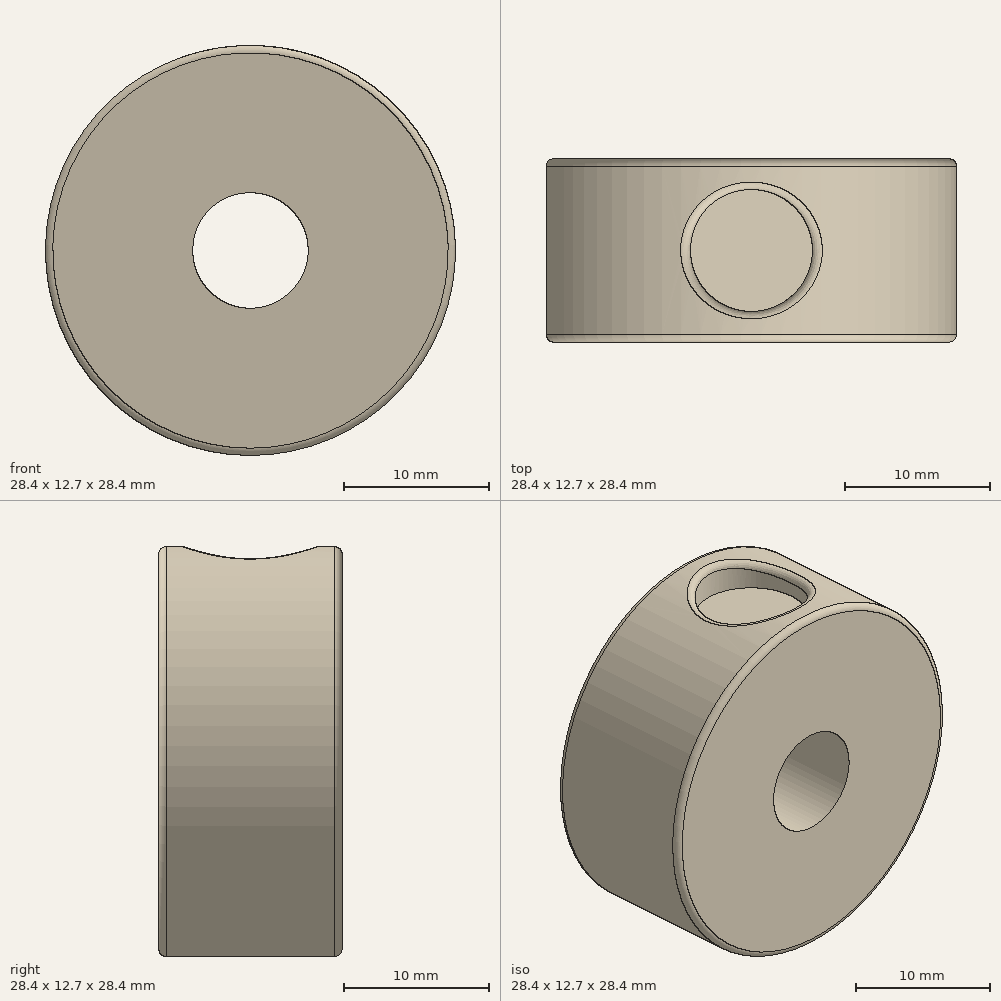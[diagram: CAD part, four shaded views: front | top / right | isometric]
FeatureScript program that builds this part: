
annotation { "Feature Type Name" : "Feature", "Feature Type Description" : "" }
export const myFeature = defineFeature(function(context is Context, id is Id, definition is map)
    precondition{}
    {
        {
            var Q0;
            Q0=qCreatedBy(makeId("Front.planeOp"),FACE);
            var sketch = newSketch(context, id + "F0", { "sketchPlane" : qUnion([Q0])});
            skCircle(sketch, "E0.cCircle", {"center": v(0, 0) * mm, "radius": 12.21 * mm, "construction": true});
            skLineSegment(sketch, "E0.0", {"start": v(-3.97, 12.21) * mm, "end": v(3.97, 12.21) * mm, "construction": true});
            skLineSegment(sketch, "E0.1", {"start": v(3.97, 12.21) * mm, "end": v(10.4, 7.55) * mm, "construction": true});
            skLineSegment(sketch, "E0.2", {"start": v(10.4, 7.55) * mm, "end": v(12.84, 0) * mm, "construction": true});
            skLineSegment(sketch, "E0.3", {"start": v(12.84, 0) * mm, "end": v(10.4, -7.55) * mm, "construction": true});
            skLineSegment(sketch, "E0.4", {"start": v(10.4, -7.55) * mm, "end": v(3.97, -12.21) * mm, "construction": true});
            skLineSegment(sketch, "E0.5", {"start": v(3.97, -12.21) * mm, "end": v(-3.97, -12.21) * mm, "construction": true});
            skLineSegment(sketch, "E0.6", {"start": v(-3.97, -12.21) * mm, "end": v(-10.4, -7.55) * mm, "construction": true});
            skLineSegment(sketch, "E0.7", {"start": v(-10.4, -7.55) * mm, "end": v(-12.84, 0) * mm, "construction": true});
            skLineSegment(sketch, "E0.8", {"start": v(-12.84, 0) * mm, "end": v(-10.4, 7.55) * mm, "construction": true});
            skLineSegment(sketch, "E0.9", {"start": v(-10.4, 7.55) * mm, "end": v(-3.97, 12.21) * mm, "construction": true});
            skPoint(sketch, "E0.0.midPoint", {"position": v(0, 12.21) * mm});
            skCircle(sketch, "E1.cCircle", {"center": v(0, 0) * mm, "radius": 14.2 * mm});
            skLineSegment(sketch, "E1.0", {"start": v(-4.61, 14.2) * mm, "end": v(4.61, 14.2) * mm, "construction": true});
            skLineSegment(sketch, "E1.1", {"start": v(4.61, 14.2) * mm, "end": v(12.08, 8.78) * mm, "construction": true});
            skLineSegment(sketch, "E1.2", {"start": v(12.08, 8.78) * mm, "end": v(14.93, 0) * mm, "construction": true});
            skLineSegment(sketch, "E1.3", {"start": v(14.93, 0) * mm, "end": v(12.08, -8.78) * mm, "construction": true});
            skLineSegment(sketch, "E1.4", {"start": v(12.08, -8.78) * mm, "end": v(4.61, -14.2) * mm, "construction": true});
            skLineSegment(sketch, "E1.5", {"start": v(4.61, -14.2) * mm, "end": v(-4.61, -14.2) * mm, "construction": true});
            skLineSegment(sketch, "E1.6", {"start": v(-4.61, -14.2) * mm, "end": v(-12.08, -8.78) * mm, "construction": true});
            skLineSegment(sketch, "E1.7", {"start": v(-12.08, -8.78) * mm, "end": v(-14.93, 0) * mm, "construction": true});
            skLineSegment(sketch, "E1.8", {"start": v(-14.93, 0) * mm, "end": v(-12.08, 8.78) * mm, "construction": true});
            skLineSegment(sketch, "E1.9", {"start": v(-12.08, 8.78) * mm, "end": v(-4.61, 14.2) * mm, "construction": true});
            skPoint(sketch, "E1.0.midPoint", {"position": v(0, 14.2) * mm});
            skCircle(sketch, "E2", {"center": v(0, 0) * mm, "radius": 4 * mm});
            skSolve(sketch);
        }
        {
            var Q0;
            Q0=qSketchRegion(id+"F0",true);
            extrude(context, id + "F1", {"entities" : qUnion([Q0]), "endBound" : BoundingType.SYMMETRIC, "depth" : 12.7 * mm});
        }
        {
            var Q0;
            Q0=qCreatedBy(makeId("Top.planeOp"),FACE);
            cPlane(context, id + "F2", {"entities" : qUnion([Q0]), "cplaneType" : CPlaneType.OFFSET, "offset" : 14.22 * mm, "width" : 152.4 * mm, "height" : 152.4 * mm});
        }
        {
            var Q0;
            Q0=qCreatedBy(id+"F2.planeOp",FACE);
            var sketch = newSketch(context, id + "F3", { "sketchPlane" : qUnion([Q0])});
            skCircle(sketch, "E3", {"center": v(0, 0) * mm, "radius": 4.22 * mm});
            skSolve(sketch);
        }
        {
            var Q0;
            Q0=qSketchRegion(id+"F3",true);
            extrude(context, id + "F4", {"entities" : qUnion([Q0]), "operationType" : NewBodyOperationType.REMOVE, "oppositeDirection" : true, "depth" : 2.5 * mm});
        }
        {
            var Q0;
            {var subQ1=sQuery(id+"F0.wireOp",EDGE,"E1.cCircle");Q0=makeQuery(id+"FT1o7iKYCXmZrac_1.boolean.opBoolean","SPLIT",FACE,{"disambiguationData":[TD([makeQuery(id+"FT1o7iKYCXmZrac_1.opRevolve","SWEPT_FACE",FACE,{"disambiguationData":[OSD([sQuery(id+"FQwpQNxOigrFaal_1.wireOp",EDGE,"1E0joroN-g8xa-gh1z-98iS-yt74jso97jHg.right")])]})])],"derivedFrom":makeQuery(id+"F1.opExtrude","SWEPT_FACE",FACE,{"disambiguationData":[OSD([subQ1])]})});}
            var Q1;
            {var subQ1=sQuery(id+"F0.wireOp",EDGE,"E1.cCircle");Q1=makeQuery(id+"FT1o7iKYCXmZrac_1.boolean.opBoolean","SPLIT",FACE,{"disambiguationData":[TD([makeQuery(id+"FT1o7iKYCXmZrac_1.opRevolve","SWEPT_FACE",FACE,{"disambiguationData":[OSD([sQuery(id+"FQwpQNxOigrFaal_1.wireOp",EDGE,"1E0joroN-g8xa-gh1z-98iS-yt74jso97jHg.left")])]})])],"derivedFrom":makeQuery(id+"F1.opExtrude","SWEPT_FACE",FACE,{"disambiguationData":[OSD([subQ1])]})});}
            fillet(context, id + "F5", {"entities" : qUnion([Q0, Q1]), "radius" : 0.5 * mm, "tangentPropagation" : true, "allowEdgeOverflow" : false});
        }
    });
